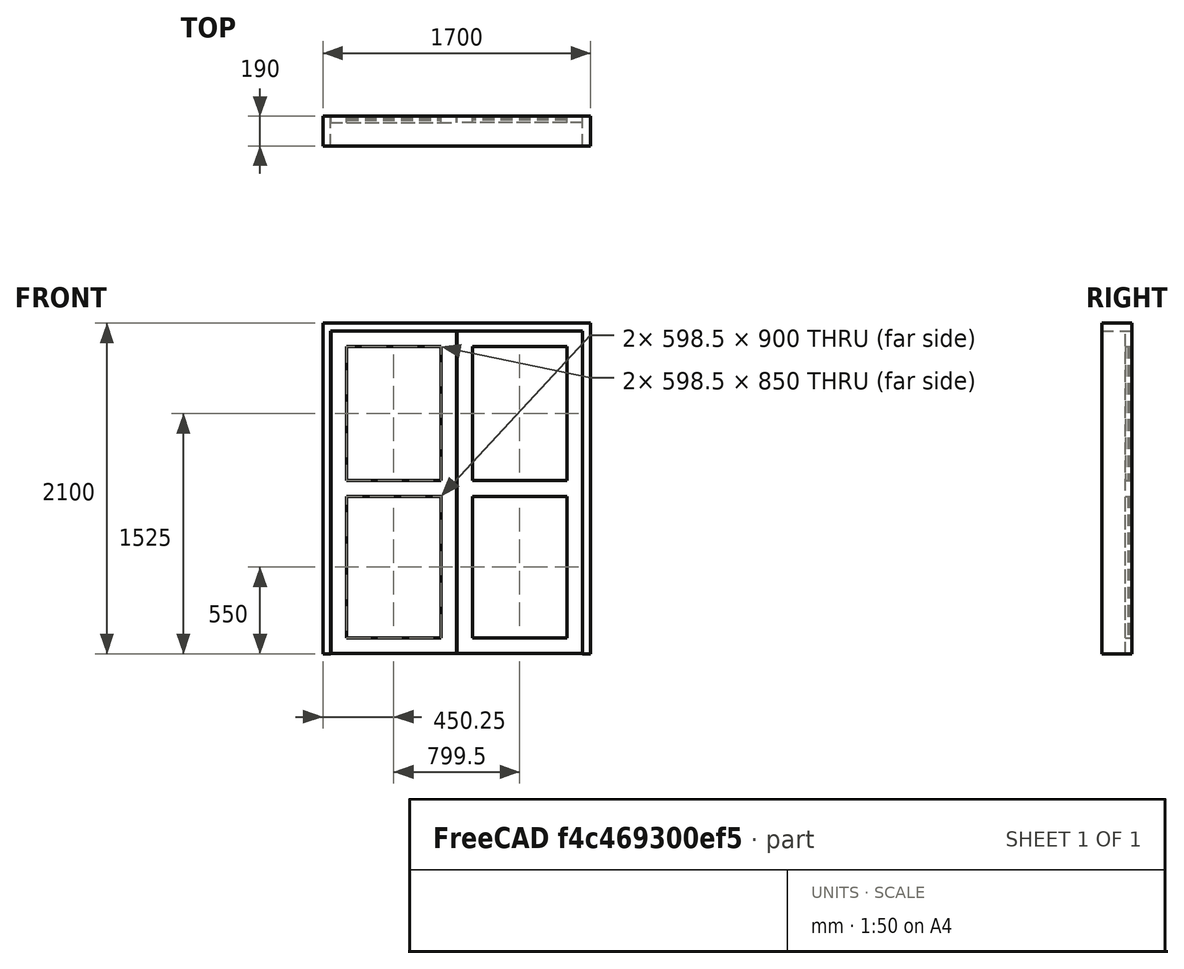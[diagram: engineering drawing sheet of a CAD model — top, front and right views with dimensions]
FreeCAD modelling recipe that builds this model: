
FCSTD DOCUMENT  (FreeCAD 0.16R6704 (Git))
Label: Double doors with glass
License: CreativeCommons Attribution
LicenseURL: http://creativecommons.org/licenses/by/4.0/
objects: Sketcher::SketchObject×1, Part::FeaturePython×1
note: 2 computed .brp shape members not serialized (recipe doc carries the construction recipe); baked Part::Feature solids carry a one-line shape summary decoded from their .brp

FEATURE [Sketcher::SketchObject] Sketch175
  Placement = pos=(0,0,0) rot=(1,0,0;1.5708rad)
  sketch-geometry (34):
    g0: LineSegment StartX=0 StartY=0 StartZ=0 EndX=1700 EndY=0 EndZ=0
    g1: LineSegment StartX=1700 StartY=0 StartZ=0 EndX=1700 EndY=2100 EndZ=0
    g2: LineSegment StartX=1700 StartY=2100 StartZ=0 EndX=0 EndY=2100 EndZ=0
    g3: LineSegment StartX=0 StartY=2100 StartZ=0 EndX=0 EndY=0 EndZ=0
    g4: LineSegment StartX=50 StartY=0 StartZ=0 EndX=1650 EndY=0 EndZ=0
    g5: LineSegment StartX=1650 StartY=0 StartZ=0 EndX=1650 EndY=2050 EndZ=0
    g6: LineSegment StartX=1650 StartY=2050 StartZ=0 EndX=50 EndY=2050 EndZ=0
    g7: LineSegment StartX=50 StartY=2050 StartZ=0 EndX=50 EndY=0 EndZ=0
    g8: LineSegment StartX=151 StartY=1950 StartZ=0 EndX=749.5 EndY=1950 EndZ=0
    g9: LineSegment StartX=749.5 StartY=1950 StartZ=0 EndX=749.5 EndY=1100 EndZ=0
    g10: LineSegment StartX=749.5 StartY=1100 StartZ=0 EndX=151 EndY=1100 EndZ=0
    g11: LineSegment StartX=151 StartY=1100 StartZ=0 EndX=151 EndY=1950 EndZ=0
    g12: LineSegment StartX=151 StartY=1000 StartZ=0 EndX=749.5 EndY=1000 EndZ=0
    g13: LineSegment StartX=749.5 StartY=1000 StartZ=0 EndX=749.5 EndY=100 EndZ=0
    g14: LineSegment StartX=749.5 StartY=100 StartZ=0 EndX=151 EndY=100 EndZ=0
    g15: LineSegment StartX=151 StartY=100 StartZ=0 EndX=151 EndY=1000 EndZ=0
    g16: LineSegment [constr] StartX=-278 StartY=1050 StartZ=0 EndX=2205 EndY=1050 EndZ=0
    g17: LineSegment StartX=51 StartY=2049 StartZ=0 EndX=849.5 EndY=2049 EndZ=0
    g18: LineSegment StartX=849.5 StartY=2049 StartZ=0 EndX=849.5 EndY=1 EndZ=0
    g19: LineSegment StartX=849.5 StartY=1 StartZ=0 EndX=51 EndY=1 EndZ=0
    g20: LineSegment StartX=51 StartY=1 StartZ=0 EndX=51 EndY=2049 EndZ=0
    g21: LineSegment [constr] StartX=850 StartY=2319.78 StartZ=0 EndX=850 EndY=-188.278 EndZ=0
    g22: LineSegment StartX=1549 StartY=1950 StartZ=0 EndX=950.5 EndY=1950 EndZ=0
    g23: LineSegment StartX=950.5 StartY=1950 StartZ=0 EndX=950.5 EndY=1100 EndZ=0
    g24: LineSegment StartX=950.5 StartY=1100 StartZ=0 EndX=1549 EndY=1100 EndZ=0
    g25: LineSegment StartX=1549 StartY=1100 StartZ=0 EndX=1549 EndY=1950 EndZ=0
    g26: LineSegment StartX=1549 StartY=1000 StartZ=0 EndX=950.5 EndY=1000 EndZ=0
    g27: LineSegment StartX=950.5 StartY=1000 StartZ=0 EndX=950.5 EndY=100 EndZ=0
    g28: LineSegment StartX=950.5 StartY=100 StartZ=0 EndX=1549 EndY=100 EndZ=0
    g29: LineSegment StartX=1549 StartY=100 StartZ=0 EndX=1549 EndY=1000 EndZ=0
    g30: LineSegment StartX=1649 StartY=2049 StartZ=0 EndX=850.5 EndY=2049 EndZ=0
    g31: LineSegment StartX=850.5 StartY=2049 StartZ=0 EndX=850.5 EndY=1 EndZ=0
    g32: LineSegment StartX=850.5 StartY=1 StartZ=0 EndX=1649 EndY=1 EndZ=0
    g33: LineSegment StartX=1649 StartY=1 StartZ=0 EndX=1649 EndY=2049 EndZ=0
  constraints (98):
    c: Coincident(g0,g1)
    c: Coincident(g1,g2)
    c: Coincident(g2,g3)
    c: Coincident(g3,g0)
    c: Horizontal(g0)
    c: Horizontal(g2)
    c: Vertical(g1)
    c: Vertical(g3)
    c: Coincident(g4,g5)
    c: Coincident(g5,g6)
    c: Coincident(g6,g7)
    c: Coincident(g7,g4)
    c: Horizontal(g4)
    c: Horizontal(g6)
    c: Vertical(g5)
    c: Vertical(g7)
    c: DistanceY(g1) = 2100  'Altura do vão'
    c: DistanceX(g0) = 1700  'Largura do vão'
    c: DistanceY(g6,g2) = 50  'Altura do batente'
    c: DistanceX(g2,g6) = 50  'Llargura do batente 1'
    c: DistanceX(g4,g0) = 50  'Batente vertical 2'
    c: Coincident(g0,g-1)
    c: Coincident(g8,g9)
    c: Coincident(g9,g10)
    c: Coincident(g10,g11)
    c: Coincident(g11,g8)
    c: Horizontal(g8)
    c: Horizontal(g10)
    c: Vertical(g9)
    c: Vertical(g11)
    c: Coincident(g12,g13)
    c: Coincident(g13,g14)
    c: Coincident(g14,g15)
    c: Coincident(g15,g12)
    c: Horizontal(g12)
    c: Horizontal(g14)
    c: Vertical(g13)
    c: Vertical(g15)
    c: DistanceX(g10,g12) = 0
    c: DistanceX(g9,g12) = 0
    c: DistanceY(g12,g10) = 100  'Montante intermediário porta'
    c: DistanceY(g8,g6) = 100  'Montante superior porta'
    c: DistanceY(g-1,g14) = 100  'Montante inferior porta'
    c: Horizontal(g16)  'Constraint44'
    c: Symmetric(g10,g12,g16)
    c: DistanceY(g-1,g16) = 1050  'Altura montante intermediário ao chão (eixo)'
    c: Coincident(g17,g18)
    c: Coincident(g18,g19)
    c: Coincident(g19,g20)
    c: Horizontal(g17)
    c: Horizontal(g19)
    c: Vertical(g18)
    c: Vertical(g20)
    c: DistanceX(g6,g17) = 1
    c: DistanceY(g17,g6) = 1  'Constraint59'
    c: DistanceX(g8,g17) = 100  'Largura montante porta 1'
    c: DistanceX(g17,g8) = 100  'Largura montante porta 2'
    c: Vertical(g21)
    c: Symmetric(g2,g1,g21)
    c: Coincident(g22,g23)
    c: Coincident(g23,g24)
    c: Coincident(g24,g25)
    c: Coincident(g25,g22)
    c: Horizontal(g22)
    c: Horizontal(g24)
    c: Vertical(g23)
    c: Vertical(g25)
    c: Coincident(g26,g27)
    c: Coincident(g27,g28)
    c: Coincident(g28,g29)
    c: Coincident(g29,g26)
    c: Horizontal(g26)
    c: Horizontal(g28)
    c: Vertical(g27)
    c: Vertical(g29)
    c: Coincident(g30,g31)
    c: Coincident(g31,g32)
    c: Coincident(g32,g33)
    c: Horizontal(g30)
    c: Horizontal(g32)
    c: Vertical(g31)
    c: Vertical(g33)
    c: DistanceX(g30,g5) = 1
    c: DistanceY(g30,g5) = 1
    c: Symmetric(g17,g30,g21)
    c: DistanceX(g17,g30) = 1
    c: DistanceY(g8,g22) = 0
    c: Symmetric(g8,g22,g21)
    c: DistanceY(g9,g23) = 0
    c: DistanceY(g26,g12) = 0
    c: Symmetric(g12,g26,g21)
    c: Symmetric(g8,g22,g21)
    c: DistanceX(g24,g26) = 0
    c: Coincident(g30,g33)
    c: DistanceY(g13,g27) = 0
    c: DistanceY(g18,g31) = 0
    c: DistanceY(g4,g19) = 1
    c: Coincident(g20,g17)
FEATURE [Part::FeaturePython] Window108  label="Double doors with glass "  # WARN: FeaturePython — macro-defined, semantics opaque (R4)
  Base = -> Sketch175
  Height = 2100
  HoleDepth = 0
  MoveWithHost = true
  Normal = (0,1,0)
  Preset = 6
  Role = 1
  Width = 900
  WindowParts = BATENTE | Frame | Wire0,Wire1 | 190.0 | 0.0 | PORTA 1 | Frame | Wire2,Wire3,Wire4 | 40.0 | 150.0 | PORTA 2 | Frame | Wire5,Wire6,Wire7 | 40.0 | 150.0 | VIDRO SUPERIOR 1 | Glass panel | Wire2 | 10.0 | 165.0 | VIDRO SUPERIOR 2 | Glass panel | Wire5 | 10.0 | 165.0 | VIDRO INFERIOR 1 | Glass panel | Wire3 | 10.0 | 165.0 | VIDRO INFERIOR 2 | Glass panel | Wire6 | 10.0 | 165.0
